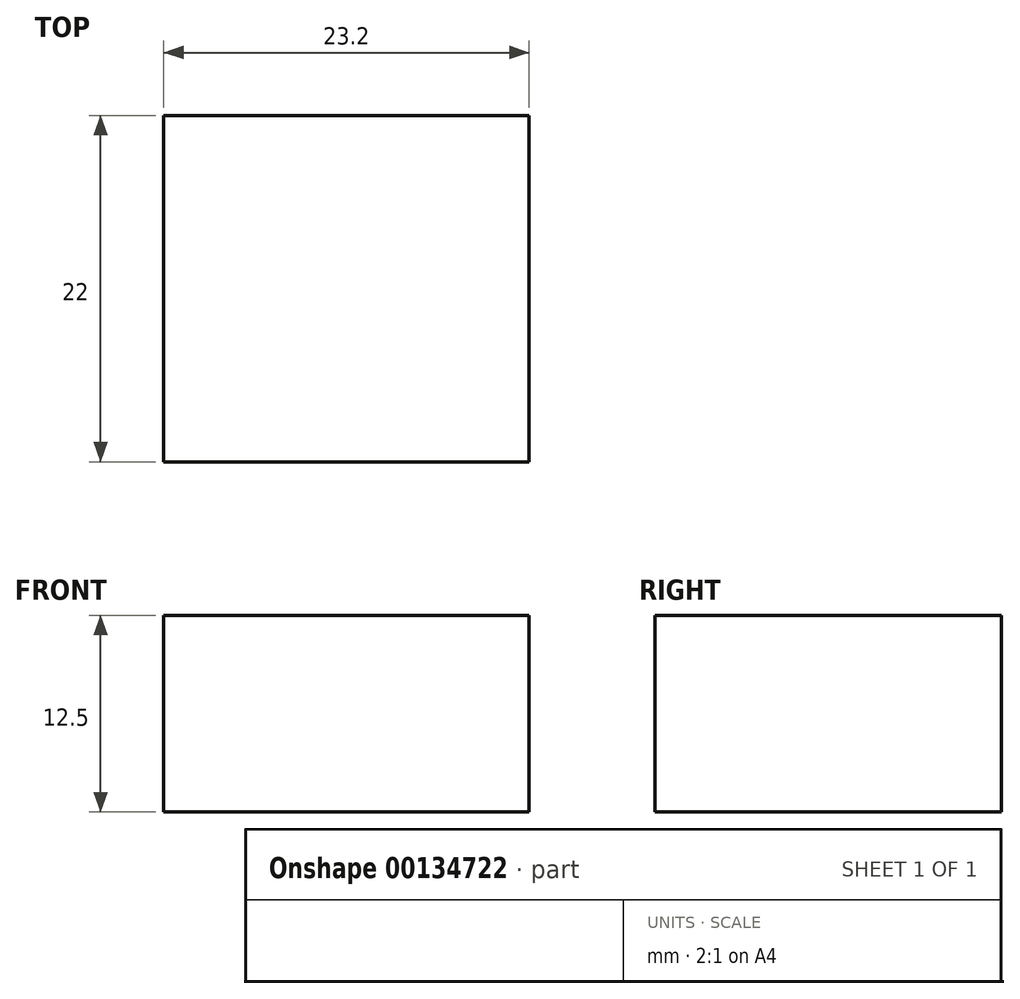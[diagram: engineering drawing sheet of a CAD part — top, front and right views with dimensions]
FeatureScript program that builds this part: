
annotation { "Feature Type Name" : "Feature", "Feature Type Description" : "" }
export const myFeature = defineFeature(function(context is Context, id is Id, definition is map)
    precondition{}
    {
        {
            var Q0;
            Q0=qCreatedBy(makeId("Front.planeOp"),FACE);
            var sketch = newSketch(context, id + "F0", { "sketchPlane" : qUnion([Q0])});
            skLineSegment(sketch, "E0.bottom", {"start": v(-21.2, 1.34) * mm, "end": v(2, 1.34) * mm});
            skLineSegment(sketch, "E0.top", {"start": v(-21.2, -11.16) * mm, "end": v(2, -11.16) * mm});
            skLineSegment(sketch, "E0.left", {"start": v(-21.2, 1.34) * mm, "end": v(-21.2, -11.16) * mm});
            skLineSegment(sketch, "E0.right", {"start": v(2, 1.34) * mm, "end": v(2, -11.16) * mm});
            skSolve(sketch);
        }
        {
            var Q0;
            Q0=makeQuery(id+"F0.imprint","IMPRINT",FACE,{"disambiguationData":[TD([[makeQuery(id+"F0.imprint","IMPRINT",EDGE,{"derivedFrom":sQuery(id+"F0.wireOp",EDGE,"E0.bottom")}),-1.0]])]});
            extrude(context, id + "F1", {"entities" : qUnion([Q0]), "depth" : 22 * mm});
        }
    });
